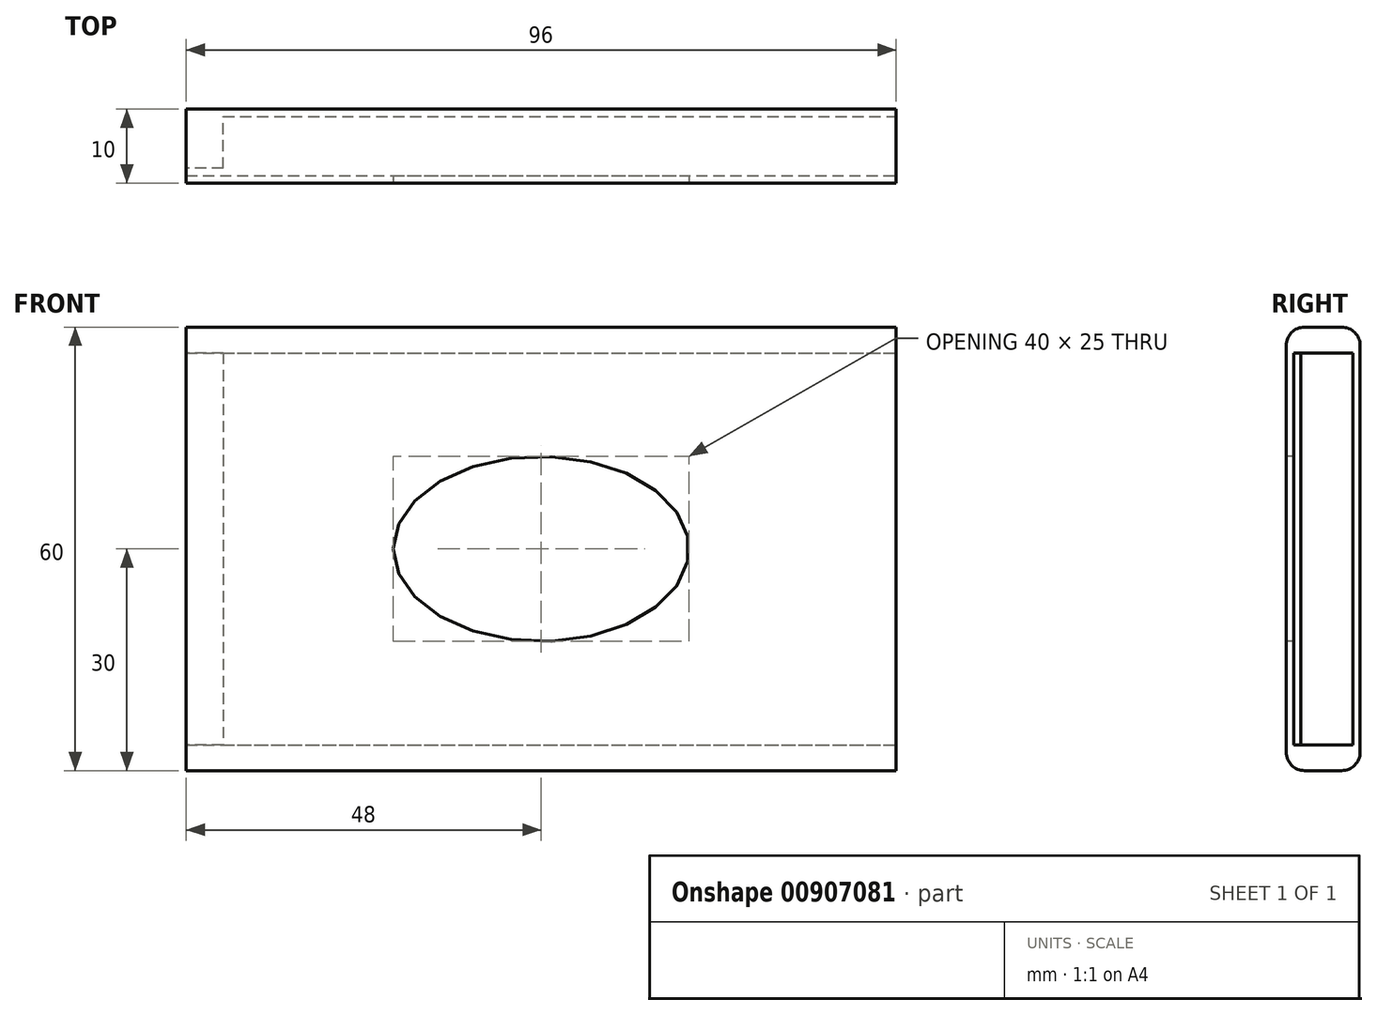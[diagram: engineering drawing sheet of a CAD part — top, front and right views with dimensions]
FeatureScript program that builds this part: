
annotation { "Feature Type Name" : "Feature", "Feature Type Description" : "" }
export const myFeature = defineFeature(function(context is Context, id is Id, definition is map)
    precondition{}
    {
        {
            var Q0;
            Q0=qCreatedBy(makeId("Right.planeOp"),FACE);
            var sketch = newSketch(context, id + "F0", { "sketchPlane" : qUnion([Q0])});
            skLineSegment(sketch, "E0.bottom", {"start": v(-5, 30) * mm, "end": v(5, 30) * mm});
            skLineSegment(sketch, "E0.top", {"start": v(-5, -30) * mm, "end": v(5, -30) * mm});
            skLineSegment(sketch, "E0.left", {"start": v(-5, 30) * mm, "end": v(-5, -30) * mm});
            skLineSegment(sketch, "E0.right", {"start": v(5, 30) * mm, "end": v(5, -30) * mm});
            skPoint(sketch, "E0.middle", {"position": v(0, 0) * mm});
            skSolve(sketch);
        }
        {
            var Q0;
            Q0=makeQuery(id+"F0.imprint","IMPRINT",FACE,{"disambiguationData":[TD([[makeQuery(id+"F0.imprint","IMPRINT",EDGE,{"derivedFrom":sQuery(id+"F0.wireOp",EDGE,"E0.bottom")}),-1.0]])]});
            extrude(context, id + "F1", {"entities" : qUnion([Q0]), "endBound" : BoundingType.SYMMETRIC, "depth" : 96 * mm, "offsetDistance" : 25 * mm});
        }
        {
            var Q0;
            Q0=makeQuery(id+"F1.opExtrude","CAP_FACE",FACE,{"disambiguationData":[OSD([sQuery(id+"F0.wireOp",EDGE,"E0.bottom"),sQuery(id+"F0.wireOp",EDGE,"E0.top"),sQuery(id+"F0.wireOp",EDGE,"E0.left"),sQuery(id+"F0.wireOp",EDGE,"E0.right")])],"isStart":false});
            var sketch = newSketch(context, id + "F2", { "sketchPlane" : qUnion([Q0])});
            skLineSegment(sketch, "E1.bottom", {"start": v(-4, 26.5) * mm, "end": v(4, 26.5) * mm});
            skLineSegment(sketch, "E1.top", {"start": v(-4, -26.5) * mm, "end": v(4, -26.5) * mm});
            skLineSegment(sketch, "E1.left", {"start": v(-4, 26.5) * mm, "end": v(-4, -26.5) * mm});
            skLineSegment(sketch, "E1.right", {"start": v(4, 26.5) * mm, "end": v(4, -26.5) * mm});
            skPoint(sketch, "E1.middle", {"position": v(0, 0) * mm});
            skSolve(sketch);
        }
        {
            var Q0;
            Q0=makeQuery(id+"F2.imprint","IMPRINT",FACE,{"disambiguationData":[TD([[makeQuery(id+"F2.imprint","IMPRINT",EDGE,{"derivedFrom":sQuery(id+"F2.wireOp",EDGE,"E1.bottom")}),-1.0]])]});
            extrude(context, id + "F3", {"entities" : qUnion([Q0]), "operationType" : NewBodyOperationType.REMOVE, "oppositeDirection" : true, "depth" : 91 * mm, "offsetDistance" : 25 * mm});
        }
        {
            var Q0;
            Q0=makeQuery(id+"F1.opExtrude","CAP_FACE",FACE,{"disambiguationData":[OSD([sQuery(id+"F0.wireOp",EDGE,"E0.bottom"),sQuery(id+"F0.wireOp",EDGE,"E0.top"),sQuery(id+"F0.wireOp",EDGE,"E0.left"),sQuery(id+"F0.wireOp",EDGE,"E0.right")])],"isStart":true});
            var sketch = newSketch(context, id + "F4", { "sketchPlane" : qUnion([Q0])});
            skLineSegment(sketch, "E2.bottom", {"start": v(3, 26.5) * mm, "end": v(4, 26.5) * mm});
            skLineSegment(sketch, "E2.top", {"start": v(3, -26.5) * mm, "end": v(4, -26.5) * mm});
            skLineSegment(sketch, "E2.left", {"start": v(3, 26.5) * mm, "end": v(3, -26.5) * mm});
            skLineSegment(sketch, "E2.right", {"start": v(4, 26.5) * mm, "end": v(4, -26.5) * mm});
            skPoint(sketch, "E2.middle", {"position": v(3.5, 0) * mm});
            skSolve(sketch);
        }
        {
            var Q0;
            Q0=makeQuery(id+"F4.imprint","IMPRINT",FACE,{"disambiguationData":[TD([[makeQuery(id+"F4.imprint","IMPRINT",EDGE,{"derivedFrom":sQuery(id+"F4.wireOp",EDGE,"E2.bottom")}),-1.0]])]});
            extrude(context, id + "F5", {"entities" : qUnion([Q0]), "operationType" : NewBodyOperationType.REMOVE, "endBound" : BoundingType.UP_TO_NEXT, "oppositeDirection" : true, "depth" : 25 * mm, "offsetDistance" : 25 * mm});
        }
        {
            var Q0;
            Q0=makeQuery(id+"F1.opExtrude","SWEPT_FACE",FACE,{"disambiguationData":[OSD([sQuery(id+"F0.wireOp",EDGE,"E0.left")])]});
            var sketch = newSketch(context, id + "F6", { "sketchPlane" : qUnion([Q0])});
            skEllipse(sketch, "E3", {"center": v(0, 0) * mm, "majorRadius": 20 * mm, "minorRadius": 12.5 * mm, "majorAxis": v(-1, 0)});
            skSolve(sketch);
        }
        {
            var Q0;
            Q0=makeQuery(id+"F6.imprint","IMPRINT",FACE,{"disambiguationData":[TD([[makeQuery(id+"F6.imprint","IMPRINT",EDGE,{"derivedFrom":sQuery(id+"F6.wireOp",EDGE,"E3")}),1.0]])]});
            extrude(context, id + "F7", {"entities" : qUnion([Q0]), "operationType" : NewBodyOperationType.REMOVE, "endBound" : BoundingType.UP_TO_NEXT, "oppositeDirection" : true, "depth" : 25 * mm, "offsetDistance" : 25 * mm});
        }
        {
            var Q0;
            Q0=makeQuery(id+"F1.opExtrude","SWEPT_EDGE",EDGE,{"disambiguationData":[OSD([sQuery(id+"F0.wireOp",EDGE,"E0.bottom"),sQuery(id+"F0.wireOp",EDGE,"E0.right")])]});
            var Q1;
            Q1=makeQuery(id+"F1.opExtrude","SWEPT_EDGE",EDGE,{"disambiguationData":[OSD([sQuery(id+"F0.wireOp",EDGE,"E0.bottom"),sQuery(id+"F0.wireOp",EDGE,"E0.left")])]});
            var Q2;
            Q2=makeQuery(id+"F1.opExtrude","SWEPT_EDGE",EDGE,{"disambiguationData":[OSD([sQuery(id+"F0.wireOp",EDGE,"E0.top"),sQuery(id+"F0.wireOp",EDGE,"E0.left")])]});
            var Q3;
            Q3=makeQuery(id+"F1.opExtrude","SWEPT_EDGE",EDGE,{"disambiguationData":[OSD([sQuery(id+"F0.wireOp",EDGE,"E0.top"),sQuery(id+"F0.wireOp",EDGE,"E0.right")])]});
            fillet(context, id + "F8", {"entities" : qUnion([Q0, Q1, Q2, Q3]), "radius" : 2.5 * mm, "tangentPropagation" : true, "allowEdgeOverflow" : false});
        }
    });
